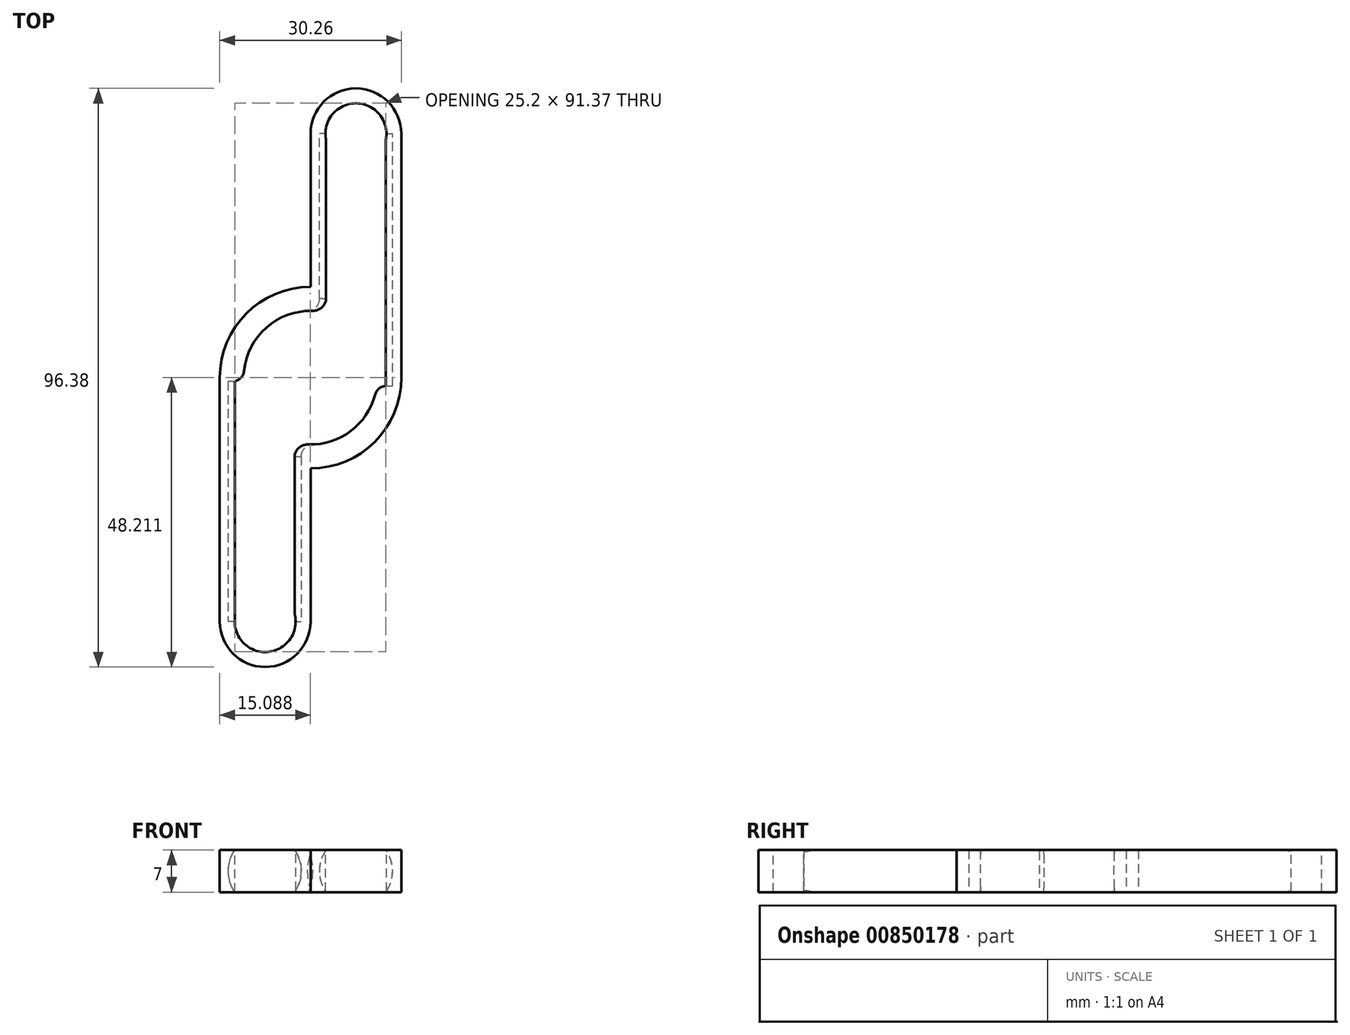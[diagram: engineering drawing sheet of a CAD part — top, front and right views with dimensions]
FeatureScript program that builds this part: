
annotation { "Feature Type Name" : "Feature", "Feature Type Description" : "" }
export const myFeature = defineFeature(function(context is Context, id is Id, definition is map)
    precondition{}
    {
        {
            var Q0;
            Q0=qCreatedBy(makeId("Top.planeOp"),FACE);
            var sketch = newSketch(context, id + "F0", { "sketchPlane" : qUnion([Q0])});
            skCircle(sketch, "E0", {"center": v(0, 0) * mm, "radius": 11.12 * mm});
            skArc(sketch, "E1", {"start": v(0, -15.12) * mm, "mid": v(10.7, -10.7) * mm, "end": v(15.12, 0) * mm});
            skLineSegment(sketch, "E2", {"start": v(0, 28.72) * mm, "end": v(0, -15.12) * mm, "construction": true});
            skLineSegment(sketch, "E3", {"start": v(-31.34, 0) * mm, "end": v(35.47, 0) * mm, "construction": true});
            skLineSegment(sketch, "E4", {"start": v(15.12, 0) * mm, "end": v(15.12, 28.86) * mm, "construction": true});
            skLineSegment(sketch, "E5", {"start": v(0, 15.12) * mm, "end": v(0, 40.62) * mm});
            skLineSegment(sketch, "E6", {"start": v(0, 40.62) * mm, "end": v(19.25, 40.62) * mm, "construction": true});
            skLineSegment(sketch, "E7", {"start": v(15.12, 0) * mm, "end": v(15.12, 40.62) * mm});
            skLineSegment(sketch, "E8", {"start": v(7.56, 40.62) * mm, "end": v(7.56, 19.86) * mm, "construction": true});
            skArc(sketch, "E9", {"start": v(15.12, 40.62) * mm, "mid": v(7.56, 48.19) * mm, "end": v(0, 40.62) * mm});
            skLineSegment(sketch, "E10.MirrorCS", {"start": v(0, -15.12) * mm, "end": v(0, -40.62) * mm});
            skLineSegment(sketch, "E11.MirrorCS", {"start": v(-15.12, 0) * mm, "end": v(-15.12, -28.86) * mm, "construction": true});
            skArc(sketch, "E12.MirrorC", {"start": v(-15.12, -40.62) * mm, "mid": v(-7.56, -48.19) * mm, "end": v(0, -40.62) * mm});
            skLineSegment(sketch, "E13.MirrorCS", {"start": v(0, -15.12) * mm, "end": v(0, -29.36) * mm});
            skLineSegment(sketch, "E14.MirrorCS", {"start": v(-15.12, 0) * mm, "end": v(-15.12, -40.62) * mm});
            skPoint(sketch, "E15.MirrorCS.end.orphan", {"position": v(15.12, -28.86) * mm});
            skPoint(sketch, "E15.MirrorCS.start.orphan", {"position": v(15.12, 0) * mm});
            skPoint(sketch, "E16.orphan", {"position": v(0, -40.62) * mm});
            skPoint(sketch, "E17.MirrorC.start.orphan", {"position": v(15.12, -40.62) * mm});
            skArc(sketch, "E18.trimOffspring", {"start": v(0, 15.12) * mm, "mid": v(-10.7, 10.7) * mm, "end": v(-15.12, 0) * mm});
            skPoint(sketch, "E19.oppositeSnap0", {"position": v(7.56, 48.19) * mm});
            skLineSegment(sketch, "E19.bottom", {"start": v(0, 40.62) * mm, "end": v(15.12, 40.62) * mm});
            skLineSegment(sketch, "E19.top", {"start": v(0, 48.19) * mm, "end": v(15.12, 48.19) * mm});
            skLineSegment(sketch, "E19.left", {"start": v(0, 40.62) * mm, "end": v(0, 48.19) * mm});
            skLineSegment(sketch, "E19.right", {"start": v(15.12, 40.62) * mm, "end": v(15.12, 48.19) * mm});
            skPoint(sketch, "E20.oppositeSnap0", {"position": v(-7.56, -48.19) * mm});
            skLineSegment(sketch, "E20.bottom", {"start": v(-15.12, -40.62) * mm, "end": v(0, -40.62) * mm});
            skLineSegment(sketch, "E20.top", {"start": v(-15.12, -48.19) * mm, "end": v(0, -48.19) * mm});
            skLineSegment(sketch, "E20.left", {"start": v(-15.12, -40.62) * mm, "end": v(-15.12, -48.19) * mm});
            skLineSegment(sketch, "E20.right", {"start": v(0, -40.62) * mm, "end": v(0, -48.19) * mm});
            skLineSegment(sketch, "E21", {"start": v(-7.56, -40.62) * mm, "end": v(-7.56, -8.16) * mm, "construction": true});
            skSolve(sketch);
        }
        {
            var Q0;
            Q0=makeQuery(id+"F0.imprint","IMPRINT",FACE,{"disambiguationData":[TD([[makeQuery(id+"F0.imprint","IMPRINT",EDGE,{"derivedFrom":sQuery(id+"F0.wireOp",EDGE,"E0")}),-1.0]])]});
            extrude(context, id + "F1", {"entities" : qUnion([Q0]), "endBound" : BoundingType.SYMMETRIC, "depth" : 7 * mm, "offsetDistance" : 25 * mm});
        }
        {
            var Q0;
            Q0=makeQuery(id+"F1.opExtrude","SWEPT_FACE",FACE,{"disambiguationData":[OSD([sQuery(id+"F0.wireOp",EDGE,"E19.bottom")])]});
            var sketch = newSketch(context, id + "F2", { "sketchPlane" : qUnion([Q0])});
            skCircle(sketch, "E22", {"center": v(-7.56, 0) * mm, "radius": 6.1 * mm});
            skPoint(sketch, "E22.centerSnap0", {"position": v(-7.56, 3.5) * mm});
            skSolve(sketch);
        }
        {
            var Q0;
            Q0 = qSketchRegion(id + "F2", true);
            extrude(context, id + "F3", {"entities" : qUnion([Q0]), "operationType" : NewBodyOperationType.REMOVE, "oppositeDirection" : true, "depth" : 42 * mm, "offsetDistance" : 25 * mm});
        }
        {
            var Q0;
            Q0=makeQuery(id+"F1.opExtrude","SWEPT_FACE",FACE,{"disambiguationData":[OSD([sQuery(id+"F0.wireOp",EDGE,"E20.bottom")])]});
            var sketch = newSketch(context, id + "F4", { "sketchPlane" : qUnion([Q0])});
            skCircle(sketch, "E23", {"center": v(-7.65, 0) * mm, "radius": 6.1 * mm});
            skSolve(sketch);
        }
        {
            var Q0;
            Q0 = qSketchRegion(id + "F4", true);
            extrude(context, id + "F5", {"entities" : qUnion([Q0]), "operationType" : NewBodyOperationType.REMOVE, "oppositeDirection" : true, "depth" : 40 * mm, "offsetDistance" : 25 * mm});
        }
        {
            var Q0;
            Q0=makeQuery(id+"F5.boolean.opBoolean","INTERSECT",EDGE,{"derivedFrom":[makeQuery(id+"F1.opExtrude","SWEPT_FACE",FACE,{"disambiguationData":[OSD([sQuery(id+"F0.wireOp",EDGE,"E0")])]}),makeQuery(id+"F5.opExtrude","CAP_FACE",FACE,{"disambiguationData":[OSD([sQuery(id+"F4.wireOp",EDGE,"E23")])],"isStart":false})]});
            var Q1;
            Q1=makeQuery(id+"F3.boolean.opBoolean","INTERSECT",EDGE,{"derivedFrom":[makeQuery(id+"F1.opExtrude","SWEPT_FACE",FACE,{"disambiguationData":[OSD([sQuery(id+"F0.wireOp",EDGE,"E0")])]}),makeQuery(id+"F3.opExtrude","CAP_FACE",FACE,{"disambiguationData":[OSD([sQuery(id+"F2.wireOp",EDGE,"E22")])],"isStart":false})]});
            var Q2;
            Q2=makeQuery(id+"F5.boolean.opBoolean","INTERSECT",EDGE,{"derivedFrom":[makeQuery(id+"F1.opExtrude","SWEPT_FACE",FACE,{"disambiguationData":[OSD([sQuery(id+"F0.wireOp",EDGE,"E0")])]}),makeQuery(id+"F5.opExtrude","SWEPT_FACE",FACE,{"disambiguationData":[OSD([sQuery(id+"F4.wireOp",EDGE,"E23")])]})]});
            var Q3;
            Q3=makeQuery(id+"F3.boolean.opBoolean","INTERSECT",EDGE,{"derivedFrom":[makeQuery(id+"F1.opExtrude","SWEPT_FACE",FACE,{"disambiguationData":[OSD([sQuery(id+"F0.wireOp",EDGE,"E0")])]}),makeQuery(id+"F3.opExtrude","SWEPT_FACE",FACE,{"disambiguationData":[OSD([sQuery(id+"F2.wireOp",EDGE,"E22")])]})]});
            fillet(context, id + "F6", {"entities" : qUnion([Q0, Q1, Q2, Q3]), "radius" : 2 * mm, "tangentPropagation" : true, "allowEdgeOverflow" : false});
        }
        {
            var Q0;
            {var subQ0=sQuery(id+"F0.wireOp",EDGE,"E20.bottom");Q0=makeQuery(id+"F0.imprint","IMPRINT",FACE,{"disambiguationData":[TD([[makeQuery(id+"F0.imprint","IMPRINT",EDGE,{"derivedFrom":subQ0}),-1.0]])]});}
            var Q1;
            {var subQ0=sQuery(id+"F0.wireOp",EDGE,"E19.bottom");Q1=makeQuery(id+"F0.imprint","IMPRINT",FACE,{"disambiguationData":[TD([[makeQuery(id+"F0.imprint","IMPRINT",EDGE,{"derivedFrom":subQ0}),1.0]])]});}
            extrude(context, id + "F7", {"entities" : qUnion([Q0, Q1]), "endBound" : BoundingType.SYMMETRIC, "depth" : 7 * mm, "offsetDistance" : 25 * mm});
        }
        {
            var Q0;
            Q0=makeQuery(id+"F7.opExtrude","SWEPT_BODY",BODY,{"disambiguationData":[OSD([sQuery(id+"F0.wireOp",EDGE,"E12.MirrorC"),sQuery(id+"F0.wireOp",EDGE,"E20.bottom")])]});
            var Q1;
            Q1=makeQuery(id+"F5.boolean.opBoolean","SPLIT",BODY,{"disambiguationData":[OD(1.0)],"derivedFrom":makeQuery(id+"F1.opExtrude","SWEPT_BODY",BODY,{"disambiguationData":[OSD([sQuery(id+"F0.wireOp",EDGE,"E0"),sQuery(id+"F0.wireOp",EDGE,"E1"),sQuery(id+"F0.wireOp",EDGE,"E5"),sQuery(id+"F0.wireOp",EDGE,"E7"),sQuery(id+"F0.wireOp",EDGE,"E10.MirrorCS"),sQuery(id+"F0.wireOp",EDGE,"E14.MirrorCS"),sQuery(id+"F0.wireOp",EDGE,"E18.trimOffspring"),sQuery(id+"F0.wireOp",EDGE,"E19.bottom"),sQuery(id+"F0.wireOp",EDGE,"E20.bottom")])]})});
            var Q2;
            Q2=makeQuery(id+"F5.boolean.opBoolean","SPLIT",BODY,{"disambiguationData":[OD(0.0)],"derivedFrom":makeQuery(id+"F1.opExtrude","SWEPT_BODY",BODY,{"disambiguationData":[OSD([sQuery(id+"F0.wireOp",EDGE,"E0"),sQuery(id+"F0.wireOp",EDGE,"E1"),sQuery(id+"F0.wireOp",EDGE,"E5"),sQuery(id+"F0.wireOp",EDGE,"E7"),sQuery(id+"F0.wireOp",EDGE,"E10.MirrorCS"),sQuery(id+"F0.wireOp",EDGE,"E14.MirrorCS"),sQuery(id+"F0.wireOp",EDGE,"E18.trimOffspring"),sQuery(id+"F0.wireOp",EDGE,"E19.bottom"),sQuery(id+"F0.wireOp",EDGE,"E20.bottom")])]})});
            var Q3;
            Q3=makeQuery(id+"F7.opExtrude","SWEPT_BODY",BODY,{"disambiguationData":[OSD([sQuery(id+"F0.wireOp",EDGE,"E9"),sQuery(id+"F0.wireOp",EDGE,"E19.bottom")])]});
            booleanBodies(context, id + "F8", {"operationType" : BooleanOperationType.UNION, "tools" : qUnion([Q0, Q1, Q2, Q3])});
        }
        {
            var Q0;
            {var subQ0=sQuery(id+"F0.wireOp",EDGE,"E20.bottom");var subQ1=sQuery(id+"F0.wireOp",EDGE,"E19.bottom");var subQ2=sQuery(id+"F0.wireOp",EDGE,"E18.trimOffspring");var subQ4=sQuery(id+"F0.wireOp",EDGE,"E14.MirrorCS");var subQ5=sQuery(id+"F0.wireOp",EDGE,"E5");var subQ6=sQuery(id+"F0.wireOp",EDGE,"E0");var subQ10=sQuery(id+"F0.wireOp",EDGE,"E10.MirrorCS");var subQ11=sQuery(id+"F0.wireOp",EDGE,"E7");var subQ12=sQuery(id+"F0.wireOp",EDGE,"E1");var subQ14=makeQuery(id+"F1.opExtrude","CAP_FACE",FACE,{"disambiguationData":[OSD([subQ6,subQ12,subQ5,subQ11,subQ10,subQ4,subQ2,subQ1,subQ0])],"isStart":false});var subQ18=subQ14;Q0=makeQuery(id+"F8.opBoolean","MERGE",FACE,{"derivedFrom":[makeQuery(id+"F5.boolean.opBoolean","SPLIT",FACE,{"disambiguationData":[TD([makeQuery(id+"F1.opExtrude","SWEPT_FACE",FACE,{"disambiguationData":[OSD([subQ12])]})])],"derivedFrom":subQ18}),makeQuery(id+"F5.boolean.opBoolean","SPLIT",FACE,{"disambiguationData":[TD([makeQuery(id+"F1.opExtrude","SWEPT_FACE",FACE,{"disambiguationData":[OSD([subQ5])]})])],"derivedFrom":subQ18}),makeQuery(id+"F7.opExtrude","CAP_FACE",FACE,{"disambiguationData":[OSD([sQuery(id+"F0.wireOp",EDGE,"E9"),subQ1])],"isStart":false}),makeQuery(id+"F7.opExtrude","CAP_FACE",FACE,{"disambiguationData":[OSD([sQuery(id+"F0.wireOp",EDGE,"E12.MirrorC"),subQ0])],"isStart":false})]});}
            var sketch = newSketch(context, id + "F9", { "sketchPlane" : qUnion([Q0])});
            skCircle(sketch, "E24", {"center": v(-7.56, -40.62) * mm, "radius": 5.08 * mm});
            skCircle(sketch, "E25.MirrorC", {"center": v(7.56, 40.62) * mm, "radius": 5.08 * mm});
            skSolve(sketch);
        }
        {
            var Q0;
            {var subQ1=sQuery(id+"F0.wireOp",EDGE,"E20.bottom");var subQ2=makeQuery(id+"F7.opExtrude","CAP_EDGE",EDGE,{"disambiguationData":[OSD([subQ1])],"isStart":false});Q0=makeQuery(id+"F9.imprint","IMPRINT",FACE,{"disambiguationData":[TD([[makeQuery(id+"F9.imprint","IMPRINT",EDGE,{"derivedFrom":subQ2}),1.0]])]});}
            var Q1;
            {var subQ2=sQuery(id+"F0.wireOp",EDGE,"E19.bottom");var subQ8=makeQuery(id+"F7.opExtrude","CAP_EDGE",EDGE,{"disambiguationData":[OSD([subQ2])],"isStart":false});Q1=makeQuery(id+"F9.imprint","IMPRINT",FACE,{"disambiguationData":[TD([[makeQuery(id+"F9.imprint","IMPRINT",EDGE,{"derivedFrom":subQ8}),-1.0]])]});}
            var Q2;
            {var subQ2=sQuery(id+"F0.wireOp",EDGE,"E19.bottom");var subQ8=makeQuery(id+"F7.opExtrude","CAP_EDGE",EDGE,{"disambiguationData":[OSD([subQ2])],"isStart":false});Q2=makeQuery(id+"F9.imprint","IMPRINT",FACE,{"disambiguationData":[TD([[makeQuery(id+"F9.imprint","IMPRINT",EDGE,{"derivedFrom":subQ8}),1.0]])]});}
            var Q3;
            {var subQ1=sQuery(id+"F0.wireOp",EDGE,"E20.bottom");var subQ2=makeQuery(id+"F7.opExtrude","CAP_EDGE",EDGE,{"disambiguationData":[OSD([subQ1])],"isStart":false});Q3=makeQuery(id+"F9.imprint","IMPRINT",FACE,{"disambiguationData":[TD([[makeQuery(id+"F9.imprint","IMPRINT",EDGE,{"derivedFrom":subQ2}),-1.0]])]});}
            extrude(context, id + "F10", {"entities" : qUnion([Q0, Q1, Q2, Q3]), "operationType" : NewBodyOperationType.REMOVE, "oppositeDirection" : true, "depth" : 25 * mm, "offsetDistance" : 25 * mm});
        }
    });
